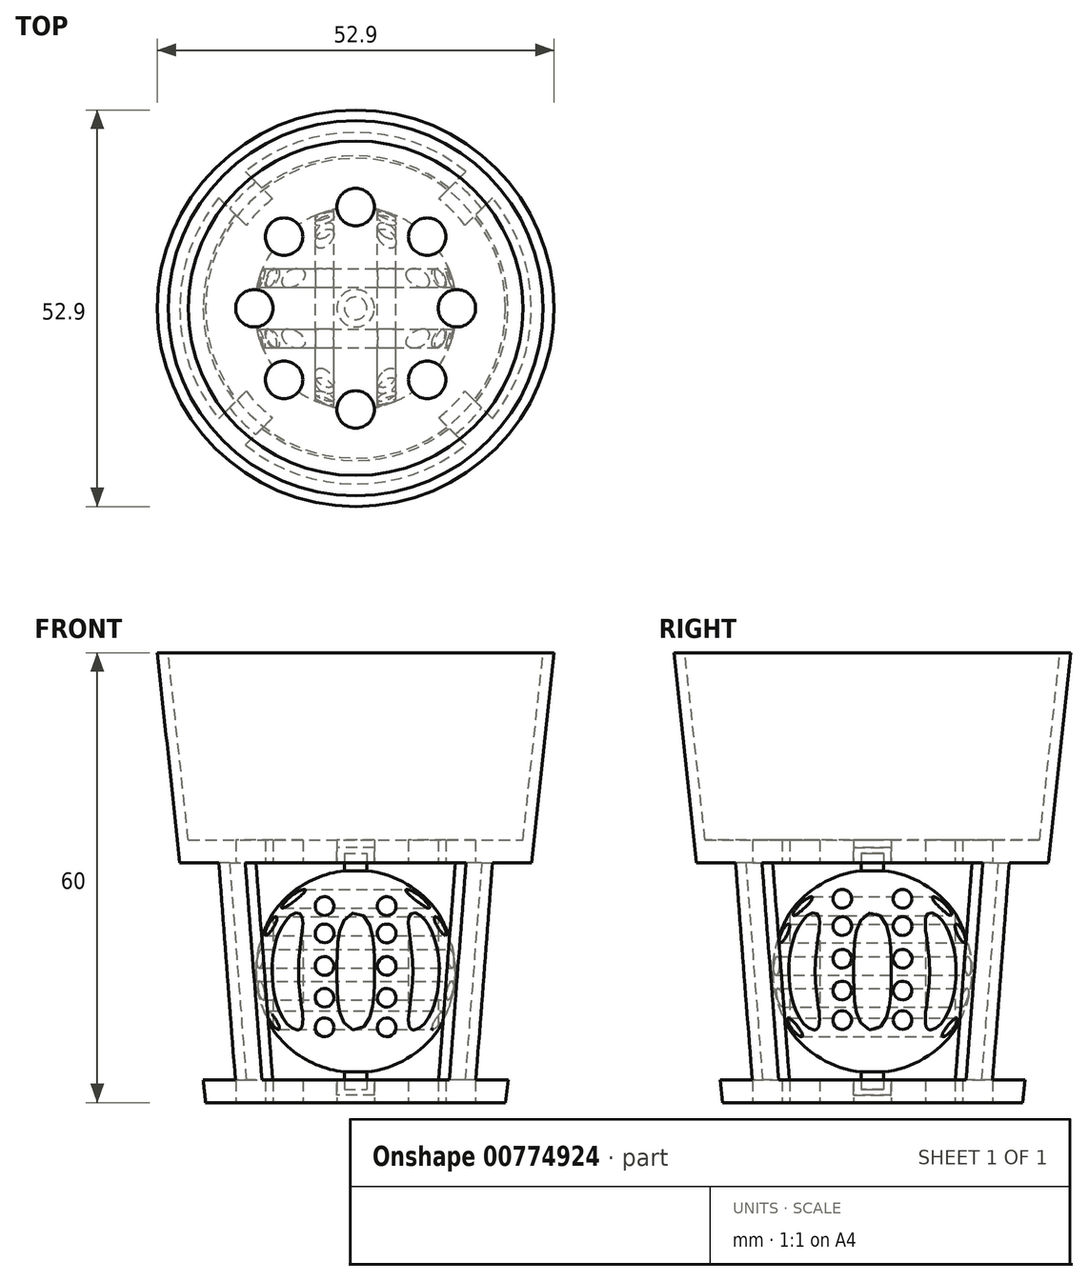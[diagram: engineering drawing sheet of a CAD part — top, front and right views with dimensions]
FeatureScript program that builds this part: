
annotation { "Feature Type Name" : "Feature", "Feature Type Description" : "" }
export const myFeature = defineFeature(function(context is Context, id is Id, definition is map)
    precondition{}
    {
        {
            var Q0;
            Q0=qCreatedBy(makeId("Front.planeOp"),FACE);
            var sketch = newSketch(context, id + "F0", { "sketchPlane" : qUnion([Q0])});
            skLineSegment(sketch, "E0", {"start": v(0, 0) * mm, "end": v(20, 0) * mm});
            skLineSegment(sketch, "E1", {"start": v(20, 0) * mm, "end": v(26.45, 60) * mm});
            skLineSegment(sketch, "E2", {"start": v(26.45, 60) * mm, "end": v(25, 60) * mm});
            skLineSegment(sketch, "E3", {"start": v(25, 60) * mm, "end": v(22.31, 35) * mm});
            skLineSegment(sketch, "E4", {"start": v(22.31, 35) * mm, "end": v(0, 35) * mm});
            skLineSegment(sketch, "E5", {"start": v(18.31, 3) * mm, "end": v(21.43, 32) * mm});
            skLineSegment(sketch, "E6", {"start": v(21.43, 32) * mm, "end": v(0, 32) * mm});
            skLineSegment(sketch, "E7", {"start": v(18.31, 3) * mm, "end": v(0, 3) * mm});
            skLineSegment(sketch, "E8.trimOffspring", {"start": v(0, 3) * mm, "end": v(0, 0) * mm});
            skLineSegment(sketch, "E9", {"start": v(0, 32) * mm, "end": v(0, 35) * mm});
            skSolve(sketch);
        }
        {
            var Q0;
            Q0 = qSketchRegion(id + "F0", true);
            var Q1;
            Q1=sQuery(id+"F0.wireOp",EDGE,"E9");
            revolve(context, id + "F1", {"surfaceOperationType" : NewSurfaceOperationType.NEW, "entities" : qUnion([Q0]), "axis" : qUnion([Q1]), "revolveType" : RevolveType.FULL});
        }
        {
            var Q0;
            Q0=makeQuery(id+"F1.opRevolve","SWEPT_FACE",FACE,{"disambiguationData":[OSD([sQuery(id+"F0.wireOp",EDGE,"E7")])]});
            var sketch = newSketch(context, id + "F2", { "sketchPlane" : qUnion([Q0])});
            skArc(sketch, "E10", {"start": v(15.68, 19.22) * mm, "mid": v(0, 24.8) * mm, "end": v(-15.68, 19.22) * mm});
            skLineSegment(sketch, "E11", {"start": v(0, 0) * mm, "end": v(0, 28.4) * mm, "construction": true});
            skLineSegment(sketch, "E12", {"start": v(0, 0) * mm, "end": v(28.58, 0) * mm, "construction": true});
            skLineSegment(sketch, "E13", {"start": v(0, 0) * mm, "end": v(20.34, 20.34) * mm, "construction": true});
            skLineSegment(sketch, "E14", {"start": v(15.8, 12.26) * mm, "end": v(19.22, 15.68) * mm});
            skLineSegment(sketch, "E15.MirrorCS", {"start": v(12.26, 15.8) * mm, "end": v(15.68, 19.22) * mm});
            skLineSegment(sketch, "E16.MirrorCS", {"start": v(-15.8, 12.26) * mm, "end": v(-19.22, 15.68) * mm});
            skLineSegment(sketch, "E17.MirrorCS", {"start": v(-12.26, 15.8) * mm, "end": v(-15.68, 19.22) * mm});
            skLineSegment(sketch, "E18.MirrorCS", {"start": v(12.26, -15.8) * mm, "end": v(15.68, -19.22) * mm});
            skLineSegment(sketch, "E19.MirrorCS", {"start": v(-12.26, -15.8) * mm, "end": v(-15.68, -19.22) * mm});
            skLineSegment(sketch, "E20.MirrorCS", {"start": v(15.8, -12.26) * mm, "end": v(19.22, -15.68) * mm});
            skLineSegment(sketch, "E21.MirrorCS", {"start": v(-15.8, -12.26) * mm, "end": v(-19.22, -15.68) * mm});
            skPoint(sketch, "E22.end.orphan", {"position": v(19.93, 19.93) * mm});
            skPoint(sketch, "E22.start.orphan", {"position": v(21.7, 18.16) * mm});
            skPoint(sketch, "E23.MirrorCS.start.orphan", {"position": v(18.16, 21.7) * mm});
            skPoint(sketch, "E24.orphan", {"position": v(-18.16, 21.7) * mm});
            skPoint(sketch, "E25.MirrorCS.end.orphan", {"position": v(-19.93, 19.93) * mm});
            skPoint(sketch, "E26.MirrorCS.start.orphan", {"position": v(-21.7, 18.16) * mm});
            skArc(sketch, "E27.trimOffspring", {"start": v(-19.22, 15.68) * mm, "mid": v(-24.8, 0) * mm, "end": v(-19.22, -15.68) * mm});
            skPoint(sketch, "E28.orphan", {"position": v(-18.16, -21.7) * mm});
            skPoint(sketch, "E29.MirrorCS.end.orphan", {"position": v(-19.93, -19.93) * mm});
            skPoint(sketch, "E30.MirrorCS.start.orphan", {"position": v(-21.7, -18.16) * mm});
            skArc(sketch, "E31.trimOffspring", {"start": v(-15.68, -19.22) * mm, "mid": v(0, -24.8) * mm, "end": v(15.68, -19.22) * mm});
            skPoint(sketch, "E32.MirrorCS.end.orphan", {"position": v(19.93, -19.93) * mm});
            skPoint(sketch, "E32.MirrorCS.start.orphan", {"position": v(21.7, -18.16) * mm});
            skPoint(sketch, "E33.MirrorCS.start.orphan", {"position": v(18.16, -21.7) * mm});
            skArc(sketch, "E34.trimOffspring", {"start": v(19.22, -15.68) * mm, "mid": v(24.8, 0) * mm, "end": v(19.22, 15.68) * mm});
            skArc(sketch, "E35", {"start": v(-14.48, 10.94) * mm, "mid": v(-18.15, 0) * mm, "end": v(-14.48, -10.94) * mm});
            skLineSegment(sketch, "E36", {"start": v(-12.26, -15.8) * mm, "end": v(-10.94, -14.48) * mm});
            skLineSegment(sketch, "E37", {"start": v(-15.8, -12.26) * mm, "end": v(-14.48, -10.94) * mm});
            skLineSegment(sketch, "E38", {"start": v(12.26, -15.8) * mm, "end": v(10.94, -14.48) * mm});
            skLineSegment(sketch, "E39", {"start": v(15.8, -12.26) * mm, "end": v(14.48, -10.94) * mm});
            skLineSegment(sketch, "E40", {"start": v(15.8, 12.26) * mm, "end": v(14.48, 10.94) * mm});
            skLineSegment(sketch, "E41", {"start": v(12.26, 15.8) * mm, "end": v(10.94, 14.48) * mm});
            skLineSegment(sketch, "E42", {"start": v(-12.26, 15.8) * mm, "end": v(-10.94, 14.48) * mm});
            skLineSegment(sketch, "E43", {"start": v(-15.8, 12.26) * mm, "end": v(-14.48, 10.94) * mm});
            skArc(sketch, "E44.trimOffspring", {"start": v(10.94, 14.48) * mm, "mid": v(0, 18.15) * mm, "end": v(-10.94, 14.48) * mm});
            skArc(sketch, "E45.trimOffspring", {"start": v(14.48, -10.94) * mm, "mid": v(18.15, 0) * mm, "end": v(14.48, 10.94) * mm});
            skArc(sketch, "E46.trimOffspring", {"start": v(-10.94, -14.48) * mm, "mid": v(0, -18.15) * mm, "end": v(10.94, -14.48) * mm});
            skSolve(sketch);
        }
        {
            var Q0;
            Q0 = qSketchRegion(id + "F2", true);
            extrude(context, id + "F3", {"entities" : qUnion([Q0]), "operationType" : NewBodyOperationType.REMOVE, "depth" : 29 * mm, "offsetDistance" : 25 * mm});
        }
        {
            var Q0;
            Q0=makeQuery(id+"F3.boolean.opBoolean","MERGE",FACE,{"derivedFrom":[makeQuery(id+"F1.opRevolve","SWEPT_FACE",FACE,{"disambiguationData":[OSD([sQuery(id+"F0.wireOp",EDGE,"E7")])]}),makeQuery(id+"F3.opExtrude","CAP_FACE",FACE,{"disambiguationData":[OSD([sQuery(id+"F2.wireOp",EDGE,"E10"),sQuery(id+"F2.wireOp",EDGE,"E15.MirrorCS"),sQuery(id+"F2.wireOp",EDGE,"E17.MirrorCS"),sQuery(id+"F2.wireOp",EDGE,"E41"),sQuery(id+"F2.wireOp",EDGE,"E42"),sQuery(id+"F2.wireOp",EDGE,"E44.trimOffspring")])],"isStart":true}),makeQuery(id+"F3.opExtrude","CAP_FACE",FACE,{"disambiguationData":[OSD([sQuery(id+"F2.wireOp",EDGE,"E14"),sQuery(id+"F2.wireOp",EDGE,"E20.MirrorCS"),sQuery(id+"F2.wireOp",EDGE,"E34.trimOffspring"),sQuery(id+"F2.wireOp",EDGE,"E39"),sQuery(id+"F2.wireOp",EDGE,"E40"),sQuery(id+"F2.wireOp",EDGE,"E45.trimOffspring")])],"isStart":true}),makeQuery(id+"F3.opExtrude","CAP_FACE",FACE,{"disambiguationData":[OSD([sQuery(id+"F2.wireOp",EDGE,"E16.MirrorCS"),sQuery(id+"F2.wireOp",EDGE,"E21.MirrorCS"),sQuery(id+"F2.wireOp",EDGE,"E27.trimOffspring"),sQuery(id+"F2.wireOp",EDGE,"E35"),sQuery(id+"F2.wireOp",EDGE,"E37"),sQuery(id+"F2.wireOp",EDGE,"E43")])],"isStart":true}),makeQuery(id+"F3.opExtrude","CAP_FACE",FACE,{"disambiguationData":[OSD([sQuery(id+"F2.wireOp",EDGE,"E18.MirrorCS"),sQuery(id+"F2.wireOp",EDGE,"E19.MirrorCS"),sQuery(id+"F2.wireOp",EDGE,"E31.trimOffspring"),sQuery(id+"F2.wireOp",EDGE,"E36"),sQuery(id+"F2.wireOp",EDGE,"E38"),sQuery(id+"F2.wireOp",EDGE,"E46.trimOffspring")])],"isStart":true})]});
            var sketch = newSketch(context, id + "F4", { "sketchPlane" : qUnion([Q0])});
            skCircle(sketch, "E47", {"center": v(0, 0) * mm, "radius": 2.5 * mm});
            skSolve(sketch);
        }
        {
            var Q0;
            Q0 = qSketchRegion(id + "F4", true);
            extrude(context, id + "F5", {"entities" : qUnion([Q0]), "operationType" : NewBodyOperationType.REMOVE, "oppositeDirection" : true, "depth" : 2 * mm, "offsetDistance" : 25 * mm, "hasSecondDirection" : true, "secondDirectionOppositeDirection" : false, "secondDirectionDepth" : 31 * mm});
        }
        {
            var Q0;
            Q0=qCreatedBy(makeId("Front.planeOp"),FACE);
            var sketch = newSketch(context, id + "F6", { "sketchPlane" : qUnion([Q0])});
            skLineSegment(sketch, "E48", {"start": v(0, 33.25) * mm, "end": v(1.5, 33.25) * mm});
            skLineSegment(sketch, "E49", {"start": v(1.5, 33.25) * mm, "end": v(1.5, 30.92) * mm});
            skLineSegment(sketch, "E50", {"start": v(1.5, 30.92) * mm, "end": v(1.5, 30.92) * mm});
            skArc(sketch, "E51", {"start": v(1.5, 4.08) * mm, "mid": v(13.5, 17.5) * mm, "end": v(1.5, 30.92) * mm});
            skLineSegment(sketch, "E52", {"start": v(1.5, 4.08) * mm, "end": v(1.5, 1.75) * mm});
            skLineSegment(sketch, "E53", {"start": v(1.5, 1.75) * mm, "end": v(0, 1.75) * mm});
            skLineSegment(sketch, "E54", {"start": v(0, 1.75) * mm, "end": v(0, 33.25) * mm});
            skSolve(sketch);
        }
        {
            var Q0;
            Q0 = qSketchRegion(id + "F6", true);
            var Q1;
            Q1=sQuery(id+"F6.wireOp",EDGE,"E54");
            revolve(context, id + "F7", {"surfaceOperationType" : NewSurfaceOperationType.NEW, "entities" : qUnion([Q0]), "axis" : qUnion([Q1]), "revolveType" : RevolveType.FULL});
        }
        {
            var Q0;
            Q0=qCreatedBy(makeId("Top.planeOp"),FACE);
            var sketch = newSketch(context, id + "F8", { "sketchPlane" : qUnion([Q0])});
            skCircle(sketch, "E55", {"center": v(0, 0) * mm, "radius": 13.5 * mm, "construction": true});
            skCircle(sketch, "E56", {"center": v(-13.5, 0) * mm, "radius": 2.5 * mm});
            skCircle(sketch, "E57.1.0", {"center": v(-9.55, -9.55) * mm, "radius": 2.5 * mm});
            skCircle(sketch, "E57.2.0", {"center": v(0, -13.5) * mm, "radius": 2.5 * mm});
            skCircle(sketch, "E57.3.0", {"center": v(9.55, -9.55) * mm, "radius": 2.5 * mm});
            skCircle(sketch, "E57.4.0", {"center": v(13.5, 0) * mm, "radius": 2.5 * mm});
            skCircle(sketch, "E57.5.0", {"center": v(9.55, 9.55) * mm, "radius": 2.5 * mm});
            skCircle(sketch, "E57.6.0", {"center": v(0, 13.5) * mm, "radius": 2.5 * mm});
            skCircle(sketch, "E57.7.0", {"center": v(-9.55, 9.55) * mm, "radius": 2.5 * mm});
            skSolve(sketch);
        }
        {
            var Q0;
            Q0 = qSketchRegion(id + "F8", true);
            extrude(context, id + "F9", {"entities" : qUnion([Q0]), "operationType" : NewBodyOperationType.REMOVE, "depth" : 36.6 * mm, "offsetDistance" : 25 * mm});
        }
        {
            var Q0;
            Q0=qCreatedBy(makeId("Right.planeOp"),FACE);
            var sketch = newSketch(context, id + "F10", { "sketchPlane" : qUnion([Q0])});
            skCircle(sketch, "E58", {"center": v(4.02, 27.18) * mm, "radius": 1.25 * mm});
            skCircle(sketch, "E59", {"center": v(4.02, 23.54) * mm, "radius": 1.25 * mm});
            skCircle(sketch, "E60", {"center": v(4.02, 19.2) * mm, "radius": 1.25 * mm});
            skCircle(sketch, "E61", {"center": v(4.02, 14.95) * mm, "radius": 1.25 * mm});
            skCircle(sketch, "E62", {"center": v(4.02, 11) * mm, "radius": 1.25 * mm});
            skCircle(sketch, "E63.MirrorC", {"center": v(-4.02, 19.2) * mm, "radius": 1.25 * mm});
            skCircle(sketch, "E64.MirrorC", {"center": v(-4.02, 14.95) * mm, "radius": 1.25 * mm});
            skCircle(sketch, "E65.MirrorC", {"center": v(-4.02, 11) * mm, "radius": 1.25 * mm});
            skCircle(sketch, "E66.MirrorC", {"center": v(-4.02, 23.54) * mm, "radius": 1.25 * mm});
            skCircle(sketch, "E67.MirrorC", {"center": v(-4.02, 27.18) * mm, "radius": 1.25 * mm});
            skSolve(sketch);
        }
        {
            var Q0;
            Q0 = qSketchRegion(id + "F10", true);
            extrude(context, id + "F11", {"entities" : qUnion([Q0]), "operationType" : NewBodyOperationType.REMOVE, "endBound" : BoundingType.SYMMETRIC, "oppositeDirection" : true, "depth" : 30 * mm, "offsetDistance" : 25 * mm});
        }
        {
            var Q0;
            Q0=qCreatedBy(makeId("Front.planeOp"),FACE);
            var sketch = newSketch(context, id + "F12", { "sketchPlane" : qUnion([Q0])});
            skCircle(sketch, "E68", {"center": v(4.14, 26.2) * mm, "radius": 1.25 * mm});
            skCircle(sketch, "E69", {"center": v(4.14, 22.57) * mm, "radius": 1.25 * mm});
            skCircle(sketch, "E70", {"center": v(4.14, 18.22) * mm, "radius": 1.25 * mm});
            skCircle(sketch, "E71", {"center": v(4.14, 13.98) * mm, "radius": 1.25 * mm});
            skCircle(sketch, "E72", {"center": v(4.14, 10.04) * mm, "radius": 1.25 * mm});
            skCircle(sketch, "E73.MirrorC", {"center": v(-4.14, 18.22) * mm, "radius": 1.25 * mm});
            skCircle(sketch, "E74.MirrorC", {"center": v(-4.14, 13.98) * mm, "radius": 1.25 * mm});
            skCircle(sketch, "E75.MirrorC", {"center": v(-4.14, 10.04) * mm, "radius": 1.25 * mm});
            skCircle(sketch, "E76.MirrorC", {"center": v(-4.14, 22.57) * mm, "radius": 1.25 * mm});
            skCircle(sketch, "E77.MirrorC", {"center": v(-4.14, 26.2) * mm, "radius": 1.25 * mm});
            skSolve(sketch);
        }
        {
            var Q0;
            Q0 = qSketchRegion(id + "F12", true);
            extrude(context, id + "F13", {"entities" : qUnion([Q0]), "operationType" : NewBodyOperationType.REMOVE, "endBound" : BoundingType.SYMMETRIC, "depth" : 30 * mm, "offsetDistance" : 25 * mm});
        }
    });
